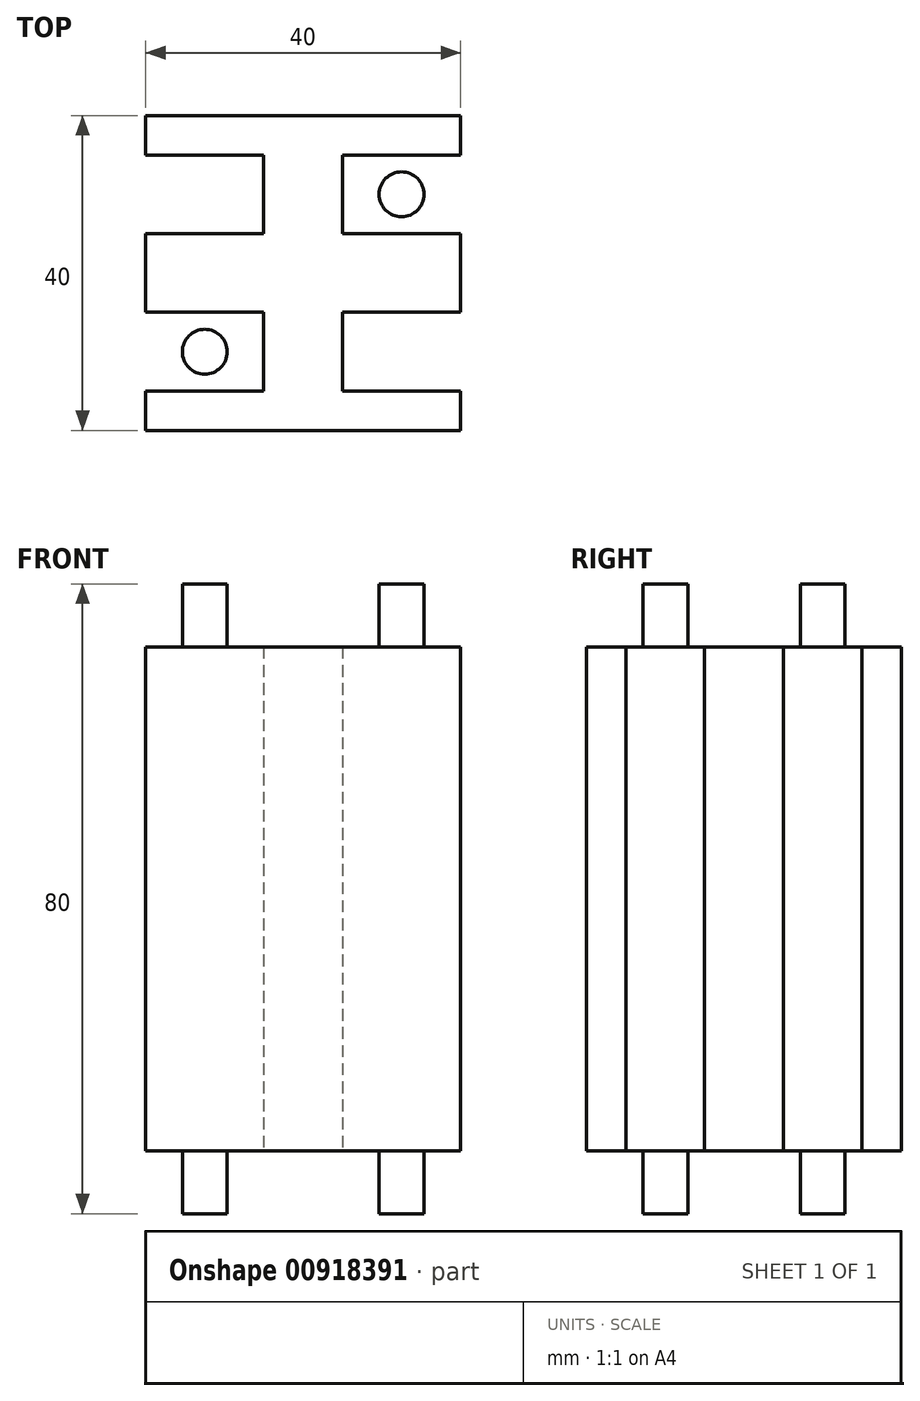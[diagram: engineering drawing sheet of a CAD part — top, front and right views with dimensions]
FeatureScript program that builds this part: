
annotation { "Feature Type Name" : "Feature", "Feature Type Description" : "" }
export const myFeature = defineFeature(function(context is Context, id is Id, definition is map)
    precondition{}
    {
        {
            var Q0;
            Q0=qCreatedBy(makeId("Top.planeOp"),FACE);
            var sketch = newSketch(context, id + "F0", { "sketchPlane" : qUnion([Q0])});
            skLineSegment(sketch, "E0.bottom", {"start": v(20, -20) * mm, "end": v(-20, -20) * mm});
            skLineSegment(sketch, "E0.top", {"start": v(20, 20) * mm, "end": v(-20, 20) * mm});
            skLineSegment(sketch, "E0.left", {"start": v(20, -20) * mm, "end": v(20, 20) * mm});
            skLineSegment(sketch, "E0.right", {"start": v(-20, -20) * mm, "end": v(-20, 20) * mm});
            skPoint(sketch, "E0.middle", {"position": v(0, 0) * mm});
            skSolve(sketch);
        }
        {
            var Q0;
            Q0=makeQuery(id+"F0.imprint","IMPRINT",FACE,{"disambiguationData":[TD([[makeQuery(id+"F0.imprint","IMPRINT",EDGE,{"derivedFrom":sQuery(id+"F0.wireOp",EDGE,"E0.bottom")}),-1.0]])]});
            extrude(context, id + "F1", {"entities" : qUnion([Q0]), "depth" : 80 * mm, "offsetDistance" : 25 * mm});
        }
        {
            var Q0;
            Q0=makeQuery(id+"F1.opExtrude","SWEPT_FACE",FACE,{"disambiguationData":[OSD([sQuery(id+"F0.wireOp",EDGE,"E0.left")])]});
            var sketch = newSketch(context, id + "F2", { "sketchPlane" : qUnion([Q0])});
            skLineSegment(sketch, "E1", {"start": v(0, 80) * mm, "end": v(0, 0) * mm, "construction": true});
            skLineSegment(sketch, "E2", {"start": v(0, 40) * mm, "end": v(-20, 40) * mm, "construction": true});
            skLineSegment(sketch, "E3", {"start": v(-10, 80) * mm, "end": v(-10, 0) * mm, "construction": true});
            skPoint(sketch, "E3.startSnap0", {"position": v(-10, 40) * mm});
            skLineSegment(sketch, "E4.0", {"start": v(-15, 80) * mm, "end": v(-15, 0) * mm});
            skLineSegment(sketch, "E5.0", {"start": v(-5, 80) * mm, "end": v(-5, 0) * mm});
            skLineSegment(sketch, "E6", {"start": v(-15, 72) * mm, "end": v(-5, 72) * mm});
            skLineSegment(sketch, "E7.MirrorCS", {"start": v(-15, 8) * mm, "end": v(-5, 8) * mm});
            skLineSegment(sketch, "E8.MirrorCS", {"start": v(15, 8) * mm, "end": v(5, 8) * mm});
            skLineSegment(sketch, "E9.MirrorCS", {"start": v(15, 80) * mm, "end": v(15, 0) * mm});
            skLineSegment(sketch, "E10.MirrorCS", {"start": v(15, 72) * mm, "end": v(5, 72) * mm});
            skLineSegment(sketch, "E11.MirrorCS", {"start": v(5, 80) * mm, "end": v(5, 0) * mm});
            skSolve(sketch);
        }
        {
            var Q0;
            {var subQ0=sQuery(id+"F2.wireOp",EDGE,"E6");Q0=makeQuery(id+"F2.imprint","IMPRINT",FACE,{"disambiguationData":[TD([[makeQuery(id+"F2.imprint","IMPRINT",EDGE,{"derivedFrom":subQ0}),-1.0]])]});}
            var Q1;
            {var subQ0=sQuery(id+"F2.wireOp",EDGE,"E8.MirrorCS");Q1=makeQuery(id+"F2.imprint","IMPRINT",FACE,{"disambiguationData":[TD([[makeQuery(id+"F2.imprint","IMPRINT",EDGE,{"derivedFrom":subQ0}),-1.0]])]});}
            extrude(context, id + "F3", {"entities" : qUnion([Q0, Q1]), "oppositeDirection" : true, "depth" : 15 * mm, "offsetDistance" : 25 * mm});
        }
        {
            var Q0;
            Q0=makeQuery(id+"F3.opExtrude","SWEPT_BODY",BODY,{"disambiguationData":[OSD([sQuery(id+"F2.wireOp",EDGE,"E8.MirrorCS"),sQuery(id+"F2.wireOp",EDGE,"E9.MirrorCS"),sQuery(id+"F2.wireOp",EDGE,"E10.MirrorCS"),sQuery(id+"F2.wireOp",EDGE,"E11.MirrorCS")])]});
            var Q1;
            Q1=makeQuery(id+"F3.opExtrude","SWEPT_BODY",BODY,{"disambiguationData":[OSD([sQuery(id+"F2.wireOp",EDGE,"E4.0"),sQuery(id+"F2.wireOp",EDGE,"E5.0"),sQuery(id+"F2.wireOp",EDGE,"E6"),sQuery(id+"F2.wireOp",EDGE,"E7.MirrorCS")])]});
            var Q2;
            Q2=qCreatedBy(makeId("Right.planeOp"),FACE);
            mirror(context, id + "F4", {"entities" : qUnion([Q0, Q1]), "mirrorPlane" : qUnion([Q2])});
        }
        {
            var Q0;
            Q0=makeQuery(id+"F3.opExtrude","SWEPT_BODY",BODY,{"disambiguationData":[OSD([sQuery(id+"F2.wireOp",EDGE,"E4.0"),sQuery(id+"F2.wireOp",EDGE,"E5.0"),sQuery(id+"F2.wireOp",EDGE,"E6"),sQuery(id+"F2.wireOp",EDGE,"E7.MirrorCS")])]});
            var Q1;
            Q1=makeQuery(id+"F3.opExtrude","SWEPT_BODY",BODY,{"disambiguationData":[OSD([sQuery(id+"F2.wireOp",EDGE,"E8.MirrorCS"),sQuery(id+"F2.wireOp",EDGE,"E9.MirrorCS"),sQuery(id+"F2.wireOp",EDGE,"E10.MirrorCS"),sQuery(id+"F2.wireOp",EDGE,"E11.MirrorCS")])]});
            var Q2;
            Q2=makeQuery(id+"F4.opPattern","COPY",BODY,{"derivedFrom":makeQuery(id+"F3.opExtrude","SWEPT_BODY",BODY,{"disambiguationData":[OSD([sQuery(id+"F2.wireOp",EDGE,"E4.0"),sQuery(id+"F2.wireOp",EDGE,"E5.0"),sQuery(id+"F2.wireOp",EDGE,"E6"),sQuery(id+"F2.wireOp",EDGE,"E7.MirrorCS")])]}),"instanceName":"1"});
            var Q3;
            Q3=makeQuery(id+"F4.opPattern","COPY",BODY,{"derivedFrom":makeQuery(id+"F3.opExtrude","SWEPT_BODY",BODY,{"disambiguationData":[OSD([sQuery(id+"F2.wireOp",EDGE,"E8.MirrorCS"),sQuery(id+"F2.wireOp",EDGE,"E9.MirrorCS"),sQuery(id+"F2.wireOp",EDGE,"E10.MirrorCS"),sQuery(id+"F2.wireOp",EDGE,"E11.MirrorCS")])]}),"instanceName":"1"});
            var Q4;
            Q4=makeQuery(id+"F1.opExtrude","SWEPT_BODY",BODY,{"disambiguationData":[OSD([sQuery(id+"F0.wireOp",EDGE,"E0.bottom"),sQuery(id+"F0.wireOp",EDGE,"E0.top"),sQuery(id+"F0.wireOp",EDGE,"E0.left"),sQuery(id+"F0.wireOp",EDGE,"E0.right")])]});
            booleanBodies(context, id + "F5", {"operationType" : BooleanOperationType.SUBTRACTION, "tools" : qUnion([Q0, Q1, Q2, Q3]), "targets" : qUnion([Q4])});
        }
        {
            var Q0;
            Q0=makeQuery(id+"F1.opExtrude","CAP_FACE",FACE,{"disambiguationData":[OSD([sQuery(id+"F0.wireOp",EDGE,"E0.bottom"),sQuery(id+"F0.wireOp",EDGE,"E0.top"),sQuery(id+"F0.wireOp",EDGE,"E0.left"),sQuery(id+"F0.wireOp",EDGE,"E0.right")])],"isStart":false});
            var sketch = newSketch(context, id + "F6", { "sketchPlane" : qUnion([Q0])});
            skLineSegment(sketch, "E12.0", {"start": v(-5, 15) * mm, "end": v(-20, 15) * mm, "construction": true});
            skLineSegment(sketch, "E12.1", {"start": v(-5, 15) * mm, "end": v(-5, 5) * mm, "construction": true});
            skLineSegment(sketch, "E12.2", {"start": v(-5, 5) * mm, "end": v(-20, 5) * mm, "construction": true});
            skCircle(sketch, "E13", {"center": v(-12.5, 10) * mm, "radius": 2.85 * mm});
            skPoint(sketch, "E13.centerSnap0", {"position": v(-5, 10) * mm});
            skPoint(sketch, "E13.centerSnap1", {"position": v(-12.5, 15) * mm});
            skCircle(sketch, "E14.MirrorC", {"center": v(12.5, 10) * mm, "radius": 2.85 * mm});
            skCircle(sketch, "E15.MirrorC", {"center": v(-12.5, -10) * mm, "radius": 2.85 * mm});
            skCircle(sketch, "E16.MirrorC", {"center": v(12.5, -10) * mm, "radius": 2.85 * mm});
            skSolve(sketch);
        }
        {
            var Q0;
            Q0=makeQuery(id+"F6.imprint","IMPRINT",FACE,{"disambiguationData":[TD([[makeQuery(id+"F6.imprint","IMPRINT",EDGE,{"derivedFrom":sQuery(id+"F6.wireOp",EDGE,"E16.MirrorC")}),1.0]])]});
            var Q1;
            Q1=makeQuery(id+"F6.imprint","IMPRINT",FACE,{"disambiguationData":[TD([[makeQuery(id+"F6.imprint","IMPRINT",EDGE,{"derivedFrom":sQuery(id+"F6.wireOp",EDGE,"E14.MirrorC")}),-1.0]])]});
            var Q2;
            Q2=makeQuery(id+"F6.imprint","IMPRINT",FACE,{"disambiguationData":[TD([[makeQuery(id+"F6.imprint","IMPRINT",EDGE,{"derivedFrom":sQuery(id+"F6.wireOp",EDGE,"E13")}),1.0]])]});
            var Q3;
            Q3=makeQuery(id+"F6.imprint","IMPRINT",FACE,{"disambiguationData":[TD([[makeQuery(id+"F6.imprint","IMPRINT",EDGE,{"derivedFrom":sQuery(id+"F6.wireOp",EDGE,"E15.MirrorC")}),-1.0]])]});
            var Q4;
            Q4=makeQuery(id+"F5.opBoolean","COPY",FACE,{"derivedFrom":makeQuery(id+"F3.opExtrude","SWEPT_FACE",FACE,{"disambiguationData":[OSD([sQuery(id+"F2.wireOp",EDGE,"E10.MirrorCS")])]})});
            extrude(context, id + "F7", {"entities" : qUnion([Q0, Q1, Q2, Q3]), "endBound" : BoundingType.UP_TO_SURFACE, "oppositeDirection" : true, "depth" : 25 * mm, "endBoundEntityFace" : qUnion([Q4]), "offsetDistance" : 25 * mm});
        }
        {
            var Q0;
            Q0=makeQuery(id+"F5.opBoolean","COPY",FACE,{"derivedFrom":makeQuery(id+"F3.opExtrude","SWEPT_FACE",FACE,{"disambiguationData":[OSD([sQuery(id+"F2.wireOp",EDGE,"E8.MirrorCS")])]})});
            var Q1;
            Q1=makeQuery(id+"F5.opBoolean","COPY",FACE,{"derivedFrom":makeQuery(id+"F3.opExtrude","SWEPT_FACE",FACE,{"disambiguationData":[OSD([sQuery(id+"F2.wireOp",EDGE,"E10.MirrorCS")])]})});
            cPlane(context, id + "F8", {"entities" : qUnion([Q0, Q1]), "cplaneType" : CPlaneType.MID_PLANE, "offset" : 25 * mm, "width" : 150 * mm, "height" : 150 * mm});
        }
        {
            var Q0;
            Q0=makeQuery(id+"F7.opExtrude","SWEPT_BODY",BODY,{"disambiguationData":[OSD([sQuery(id+"F6.wireOp",EDGE,"E13")])]});
            var Q1;
            Q1=makeQuery(id+"F7.opExtrude","SWEPT_BODY",BODY,{"disambiguationData":[OSD([sQuery(id+"F6.wireOp",EDGE,"E14.MirrorC")])]});
            var Q2;
            Q2=makeQuery(id+"F7.opExtrude","SWEPT_BODY",BODY,{"disambiguationData":[OSD([sQuery(id+"F6.wireOp",EDGE,"E15.MirrorC")])]});
            var Q3;
            Q3=makeQuery(id+"F7.opExtrude","SWEPT_BODY",BODY,{"disambiguationData":[OSD([sQuery(id+"F6.wireOp",EDGE,"E16.MirrorC")])]});
            var Q4;
            Q4=qCreatedBy(id+"F8.planeOp",FACE);
            mirror(context, id + "F9", {"entities" : qUnion([Q0, Q1, Q2, Q3]), "mirrorPlane" : qUnion([Q4])});
        }
        {
            var Q0;
            Q0=makeQuery(id+"F7.opExtrude","SWEPT_BODY",BODY,{"disambiguationData":[OSD([sQuery(id+"F6.wireOp",EDGE,"E13")])]});
            var Q1;
            Q1=makeQuery(id+"F7.opExtrude","SWEPT_BODY",BODY,{"disambiguationData":[OSD([sQuery(id+"F6.wireOp",EDGE,"E14.MirrorC")])]});
            var Q2;
            Q2=makeQuery(id+"F7.opExtrude","SWEPT_BODY",BODY,{"disambiguationData":[OSD([sQuery(id+"F6.wireOp",EDGE,"E15.MirrorC")])]});
            var Q3;
            Q3=makeQuery(id+"F7.opExtrude","SWEPT_BODY",BODY,{"disambiguationData":[OSD([sQuery(id+"F6.wireOp",EDGE,"E16.MirrorC")])]});
            var Q4;
            Q4=makeQuery(id+"F9.opPattern","COPY",BODY,{"derivedFrom":makeQuery(id+"F7.opExtrude","SWEPT_BODY",BODY,{"disambiguationData":[OSD([sQuery(id+"F6.wireOp",EDGE,"E13")])]}),"instanceName":"1"});
            var Q5;
            Q5=makeQuery(id+"F9.opPattern","COPY",BODY,{"derivedFrom":makeQuery(id+"F7.opExtrude","SWEPT_BODY",BODY,{"disambiguationData":[OSD([sQuery(id+"F6.wireOp",EDGE,"E14.MirrorC")])]}),"instanceName":"1"});
            var Q6;
            Q6=makeQuery(id+"F9.opPattern","COPY",BODY,{"derivedFrom":makeQuery(id+"F7.opExtrude","SWEPT_BODY",BODY,{"disambiguationData":[OSD([sQuery(id+"F6.wireOp",EDGE,"E15.MirrorC")])]}),"instanceName":"1"});
            var Q7;
            Q7=makeQuery(id+"F9.opPattern","COPY",BODY,{"derivedFrom":makeQuery(id+"F7.opExtrude","SWEPT_BODY",BODY,{"disambiguationData":[OSD([sQuery(id+"F6.wireOp",EDGE,"E16.MirrorC")])]}),"instanceName":"1"});
            var Q8;
            Q8=makeQuery(id+"F1.opExtrude","SWEPT_BODY",BODY,{"disambiguationData":[OSD([sQuery(id+"F0.wireOp",EDGE,"E0.bottom"),sQuery(id+"F0.wireOp",EDGE,"E0.top"),sQuery(id+"F0.wireOp",EDGE,"E0.left"),sQuery(id+"F0.wireOp",EDGE,"E0.right")])]});
            booleanBodies(context, id + "F10", {"operationType" : BooleanOperationType.SUBTRACTION, "tools" : qUnion([Q0, Q1, Q2, Q3, Q4, Q5, Q6, Q7]), "targets" : qUnion([Q8])});
        }
    });
